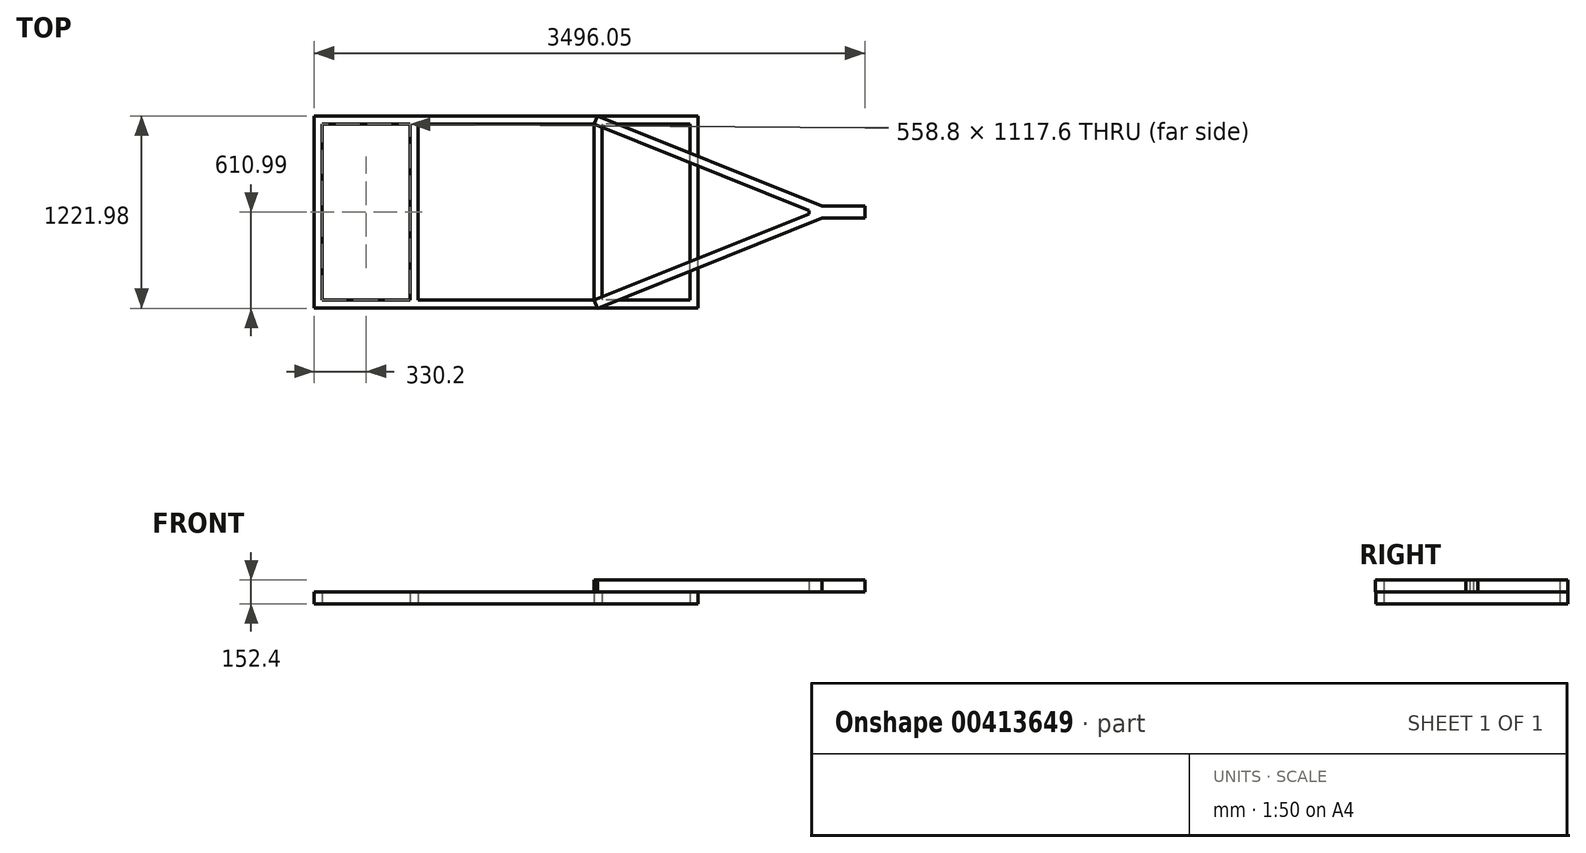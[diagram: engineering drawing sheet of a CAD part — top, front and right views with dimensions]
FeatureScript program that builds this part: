
annotation { "Feature Type Name" : "Feature", "Feature Type Description" : "" }
export const myFeature = defineFeature(function(context is Context, id is Id, definition is map)
    precondition{}
    {
        {
            var Q0;
            Q0=qCreatedBy(makeId("Top.planeOp"),FACE);
            var sketch = newSketch(context, id + "F0", { "sketchPlane" : qUnion([Q0])});
            skLineSegment(sketch, "E0.bottom", {"start": v(1219.2, -609.6) * mm, "end": v(-1219.2, -609.6) * mm});
            skLineSegment(sketch, "E0.top", {"start": v(1219.2, 609.6) * mm, "end": v(-1219.2, 609.6) * mm});
            skLineSegment(sketch, "E0.left", {"start": v(1219.2, -609.6) * mm, "end": v(1219.2, 609.6) * mm});
            skLineSegment(sketch, "E0.right", {"start": v(-1219.2, -609.6) * mm, "end": v(-1219.2, 609.6) * mm});
            skPoint(sketch, "E0.middle", {"position": v(0, 0) * mm});
            skLineSegment(sketch, "E1", {"start": v(-609.6, -609.6) * mm, "end": v(-609.6, 609.6) * mm});
            skLineSegment(sketch, "E2", {"start": v(609.6, 609.6) * mm, "end": v(609.6, -609.6) * mm});
            skLineSegment(sketch, "E3.0", {"start": v(-1168.4, -609.6) * mm, "end": v(-1168.4, 609.6) * mm});
            skLineSegment(sketch, "E4.0", {"start": v(1168.4, -609.6) * mm, "end": v(1168.4, 609.6) * mm});
            skLineSegment(sketch, "E5.0", {"start": v(1219.2, -558.8) * mm, "end": v(-1219.2, -558.8) * mm});
            skLineSegment(sketch, "E6.0", {"start": v(1219.2, 558.8) * mm, "end": v(-1219.2, 558.8) * mm});
            skLineSegment(sketch, "E7.0", {"start": v(-558.8, -609.6) * mm, "end": v(-558.8, 609.6) * mm});
            skLineSegment(sketch, "E8.0", {"start": v(558.8, 609.6) * mm, "end": v(558.8, -609.6) * mm});
            skSolve(sketch);
        }
        {
            var Q0;
            {var subQ0=sQuery(id+"F0.wireOp",EDGE,"E6.0");var subQ1=sQuery(id+"F0.wireOp",EDGE,"E2");var subQ2=makeQuery(id+"F0.imprint","INTERSECT",VERTEX,{"derivedFrom":[subQ1,subQ0]});Q0=makeQuery(id+"F0.imprint","IMPRINT",FACE,{"disambiguationData":[TD([[makeQuery(id+"F0.imprint","IMPRINT",EDGE,{"disambiguationData":[TD([[subQ2,-1.0]])],"derivedFrom":subQ1}),-1.0]])]});}
            var Q1;
            {var subQ0=sQuery(id+"F0.wireOp",EDGE,"E2");var subQ1=sQuery(id+"F0.wireOp",EDGE,"E0.bottom");var subQ2=makeQuery(id+"F0.imprint","INTERSECT",VERTEX,{"derivedFrom":[subQ1,subQ0]});Q1=makeQuery(id+"F0.imprint","IMPRINT",FACE,{"disambiguationData":[TD([[makeQuery(id+"F0.imprint","IMPRINT",EDGE,{"disambiguationData":[TD([[subQ2,-1.0]])],"derivedFrom":subQ1}),-1.0]])]});}
            var Q2;
            {var subQ0=sQuery(id+"F0.wireOp",EDGE,"E2");var subQ1=sQuery(id+"F0.wireOp",EDGE,"E0.bottom");var subQ2=makeQuery(id+"F0.imprint","INTERSECT",VERTEX,{"derivedFrom":[subQ1,subQ0]});Q2=makeQuery(id+"F0.imprint","IMPRINT",FACE,{"disambiguationData":[TD([[makeQuery(id+"F0.imprint","IMPRINT",EDGE,{"disambiguationData":[TD([[subQ2,1.0]])],"derivedFrom":subQ1}),-1.0]])]});}
            var Q3;
            {var subQ0=sQuery(id+"F0.wireOp",EDGE,"E7.0");var subQ1=sQuery(id+"F0.wireOp",EDGE,"E0.bottom");var subQ2=makeQuery(id+"F0.imprint","INTERSECT",VERTEX,{"derivedFrom":[subQ1,subQ0]});Q3=makeQuery(id+"F0.imprint","IMPRINT",FACE,{"disambiguationData":[TD([[makeQuery(id+"F0.imprint","IMPRINT",EDGE,{"disambiguationData":[TD([[subQ2,1.0]])],"derivedFrom":subQ1}),-1.0]])]});}
            var Q4;
            {var subQ0=sQuery(id+"F0.wireOp",EDGE,"E1");var subQ1=sQuery(id+"F0.wireOp",EDGE,"E0.bottom");var subQ2=makeQuery(id+"F0.imprint","INTERSECT",VERTEX,{"derivedFrom":[subQ1,subQ0]});Q4=makeQuery(id+"F0.imprint","IMPRINT",FACE,{"disambiguationData":[TD([[makeQuery(id+"F0.imprint","IMPRINT",EDGE,{"disambiguationData":[TD([[subQ2,1.0]])],"derivedFrom":subQ1}),-1.0]])]});}
            var Q5;
            {var subQ0=sQuery(id+"F0.wireOp",EDGE,"E5.0");var subQ1=sQuery(id+"F0.wireOp",EDGE,"E1");var subQ2=makeQuery(id+"F0.imprint","INTERSECT",VERTEX,{"derivedFrom":[subQ1,subQ0]});Q5=makeQuery(id+"F0.imprint","IMPRINT",FACE,{"disambiguationData":[TD([[makeQuery(id+"F0.imprint","IMPRINT",EDGE,{"disambiguationData":[TD([[subQ2,-1.0]])],"derivedFrom":subQ1}),-1.0]])]});}
            var Q6;
            {var subQ0=sQuery(id+"F0.wireOp",EDGE,"E1");var subQ1=sQuery(id+"F0.wireOp",EDGE,"E0.bottom");var subQ2=makeQuery(id+"F0.imprint","INTERSECT",VERTEX,{"derivedFrom":[subQ1,subQ0]});Q6=makeQuery(id+"F0.imprint","IMPRINT",FACE,{"disambiguationData":[TD([[makeQuery(id+"F0.imprint","IMPRINT",EDGE,{"disambiguationData":[TD([[subQ2,-1.0]])],"derivedFrom":subQ1}),-1.0]])]});}
            var Q7;
            {var subQ0=sQuery(id+"F0.wireOp",EDGE,"E0.right");var subQ1=sQuery(id+"F0.wireOp",EDGE,"E0.bottom");var subQ2=makeQuery(id+"F0.imprint","INTERSECT",VERTEX,{"derivedFrom":[subQ1,subQ0]});Q7=makeQuery(id+"F0.imprint","IMPRINT",FACE,{"disambiguationData":[TD([[makeQuery(id+"F0.imprint","IMPRINT",EDGE,{"disambiguationData":[TD([[subQ2,1.0]])],"derivedFrom":subQ1}),-1.0]])]});}
            var Q8;
            {var subQ0=sQuery(id+"F0.wireOp",EDGE,"E5.0");var subQ1=sQuery(id+"F0.wireOp",EDGE,"E0.right");var subQ2=makeQuery(id+"F0.imprint","INTERSECT",VERTEX,{"derivedFrom":[subQ1,subQ0]});Q8=makeQuery(id+"F0.imprint","IMPRINT",FACE,{"disambiguationData":[TD([[makeQuery(id+"F0.imprint","IMPRINT",EDGE,{"disambiguationData":[TD([[subQ2,-1.0]])],"derivedFrom":subQ1}),-1.0]])]});}
            var Q9;
            {var subQ0=sQuery(id+"F0.wireOp",EDGE,"E0.right");var subQ1=sQuery(id+"F0.wireOp",EDGE,"E0.top");var subQ2=makeQuery(id+"F0.imprint","INTERSECT",VERTEX,{"derivedFrom":[subQ1,subQ0]});Q9=makeQuery(id+"F0.imprint","IMPRINT",FACE,{"disambiguationData":[TD([[makeQuery(id+"F0.imprint","IMPRINT",EDGE,{"disambiguationData":[TD([[subQ2,1.0]])],"derivedFrom":subQ1}),1.0]])]});}
            var Q10;
            {var subQ0=sQuery(id+"F0.wireOp",EDGE,"E1");var subQ1=sQuery(id+"F0.wireOp",EDGE,"E0.top");var subQ2=makeQuery(id+"F0.imprint","INTERSECT",VERTEX,{"derivedFrom":[subQ1,subQ0]});Q10=makeQuery(id+"F0.imprint","IMPRINT",FACE,{"disambiguationData":[TD([[makeQuery(id+"F0.imprint","IMPRINT",EDGE,{"disambiguationData":[TD([[subQ2,-1.0]])],"derivedFrom":subQ1}),1.0]])]});}
            var Q11;
            {var subQ0=sQuery(id+"F0.wireOp",EDGE,"E7.0");var subQ1=sQuery(id+"F0.wireOp",EDGE,"E0.top");var subQ2=makeQuery(id+"F0.imprint","INTERSECT",VERTEX,{"derivedFrom":[subQ1,subQ0]});Q11=makeQuery(id+"F0.imprint","IMPRINT",FACE,{"disambiguationData":[TD([[makeQuery(id+"F0.imprint","IMPRINT",EDGE,{"disambiguationData":[TD([[subQ2,1.0]])],"derivedFrom":subQ1}),1.0]])]});}
            var Q12;
            {var subQ0=sQuery(id+"F0.wireOp",EDGE,"E1");var subQ1=sQuery(id+"F0.wireOp",EDGE,"E0.top");var subQ2=makeQuery(id+"F0.imprint","INTERSECT",VERTEX,{"derivedFrom":[subQ1,subQ0]});Q12=makeQuery(id+"F0.imprint","IMPRINT",FACE,{"disambiguationData":[TD([[makeQuery(id+"F0.imprint","IMPRINT",EDGE,{"disambiguationData":[TD([[subQ2,1.0]])],"derivedFrom":subQ1}),1.0]])]});}
            var Q13;
            {var subQ0=sQuery(id+"F0.wireOp",EDGE,"E2");var subQ1=sQuery(id+"F0.wireOp",EDGE,"E0.top");var subQ2=makeQuery(id+"F0.imprint","INTERSECT",VERTEX,{"derivedFrom":[subQ1,subQ0]});Q13=makeQuery(id+"F0.imprint","IMPRINT",FACE,{"disambiguationData":[TD([[makeQuery(id+"F0.imprint","IMPRINT",EDGE,{"disambiguationData":[TD([[subQ2,-1.0]])],"derivedFrom":subQ1}),1.0]])]});}
            var Q14;
            {var subQ0=sQuery(id+"F0.wireOp",EDGE,"E2");var subQ1=sQuery(id+"F0.wireOp",EDGE,"E0.top");var subQ2=makeQuery(id+"F0.imprint","INTERSECT",VERTEX,{"derivedFrom":[subQ1,subQ0]});Q14=makeQuery(id+"F0.imprint","IMPRINT",FACE,{"disambiguationData":[TD([[makeQuery(id+"F0.imprint","IMPRINT",EDGE,{"disambiguationData":[TD([[subQ2,1.0]])],"derivedFrom":subQ1}),1.0]])]});}
            var Q15;
            {var subQ0=sQuery(id+"F0.wireOp",EDGE,"E0.left");var subQ1=sQuery(id+"F0.wireOp",EDGE,"E0.top");var subQ2=makeQuery(id+"F0.imprint","INTERSECT",VERTEX,{"derivedFrom":[subQ1,subQ0]});Q15=makeQuery(id+"F0.imprint","IMPRINT",FACE,{"disambiguationData":[TD([[makeQuery(id+"F0.imprint","IMPRINT",EDGE,{"disambiguationData":[TD([[subQ2,-1.0]])],"derivedFrom":subQ1}),1.0]])]});}
            var Q16;
            {var subQ0=sQuery(id+"F0.wireOp",EDGE,"E5.0");var subQ1=sQuery(id+"F0.wireOp",EDGE,"E0.left");var subQ2=makeQuery(id+"F0.imprint","INTERSECT",VERTEX,{"derivedFrom":[subQ1,subQ0]});Q16=makeQuery(id+"F0.imprint","IMPRINT",FACE,{"disambiguationData":[TD([[makeQuery(id+"F0.imprint","IMPRINT",EDGE,{"disambiguationData":[TD([[subQ2,-1.0]])],"derivedFrom":subQ1}),1.0]])]});}
            var Q17;
            {var subQ0=sQuery(id+"F0.wireOp",EDGE,"E0.left");var subQ1=sQuery(id+"F0.wireOp",EDGE,"E0.bottom");var subQ2=makeQuery(id+"F0.imprint","INTERSECT",VERTEX,{"derivedFrom":[subQ1,subQ0]});Q17=makeQuery(id+"F0.imprint","IMPRINT",FACE,{"disambiguationData":[TD([[makeQuery(id+"F0.imprint","IMPRINT",EDGE,{"disambiguationData":[TD([[subQ2,-1.0]])],"derivedFrom":subQ1}),-1.0]])]});}
            extrude(context, id + "F1", {"entities" : qUnion([Q0, Q1, Q2, Q3, Q4, Q5, Q6, Q7, Q8, Q9, Q10, Q11, Q12, Q13, Q14, Q15, Q16, Q17]), "depth" : 76.2 * mm});
        }
        {
            var Q0;
            Q0=makeQuery(id+"F1.opExtrude","CAP_FACE",FACE,{"disambiguationData":[OSD([sQuery(id+"F0.wireOp",EDGE,"E0.bottom"),sQuery(id+"F0.wireOp",EDGE,"E0.top"),sQuery(id+"F0.wireOp",EDGE,"E0.left"),sQuery(id+"F0.wireOp",EDGE,"E0.right"),sQuery(id+"F0.wireOp",EDGE,"E1"),sQuery(id+"F0.wireOp",EDGE,"E2"),sQuery(id+"F0.wireOp",EDGE,"E3.0"),sQuery(id+"F0.wireOp",EDGE,"E4.0"),sQuery(id+"F0.wireOp",EDGE,"E5.0"),sQuery(id+"F0.wireOp",EDGE,"E6.0"),sQuery(id+"F0.wireOp",EDGE,"E7.0"),sQuery(id+"F0.wireOp",EDGE,"E8.0")])],"isStart":false});
            var sketch = newSketch(context, id + "F2", { "sketchPlane" : qUnion([Q0])});
            skLineSegment(sketch, "E9", {"start": v(558.8, 558.8) * mm, "end": v(1948.28, 0) * mm});
            skLineSegment(sketch, "E10", {"start": v(1948.28, 0) * mm, "end": v(558.8, -558.8) * mm});
            skLineSegment(sketch, "E11.0", {"start": v(2099.05, 0) * mm, "end": v(579.8, -611) * mm});
            skLineSegment(sketch, "E11.1", {"start": v(579.8, 611) * mm, "end": v(2099.05, 0) * mm});
            skLineSegment(sketch, "E12", {"start": v(558.8, -558.8) * mm, "end": v(579.8, -611) * mm});
            skLineSegment(sketch, "E13", {"start": v(579.8, 611) * mm, "end": v(558.8, 558.8) * mm});
            skLineSegment(sketch, "E14.bottom", {"start": v(2276.85, -38.1) * mm, "end": v(1921.25, -38.1) * mm});
            skLineSegment(sketch, "E14.top", {"start": v(2276.85, 38.1) * mm, "end": v(1921.25, 38.1) * mm});
            skLineSegment(sketch, "E14.left", {"start": v(2276.85, -38.1) * mm, "end": v(2276.85, 38.1) * mm});
            skLineSegment(sketch, "E14.right", {"start": v(1921.25, -38.1) * mm, "end": v(1921.25, 38.1) * mm});
            skPoint(sketch, "E14.middle", {"position": v(2099.05, 0) * mm});
            skSolve(sketch);
        }
        {
            var Q0;
            Q0 = qSketchRegion(id + "F2", true);
            extrude(context, id + "F3", {"entities" : qUnion([Q0]), "operationType" : NewBodyOperationType.ADD, "depth" : 76.2 * mm});
        }
    });
